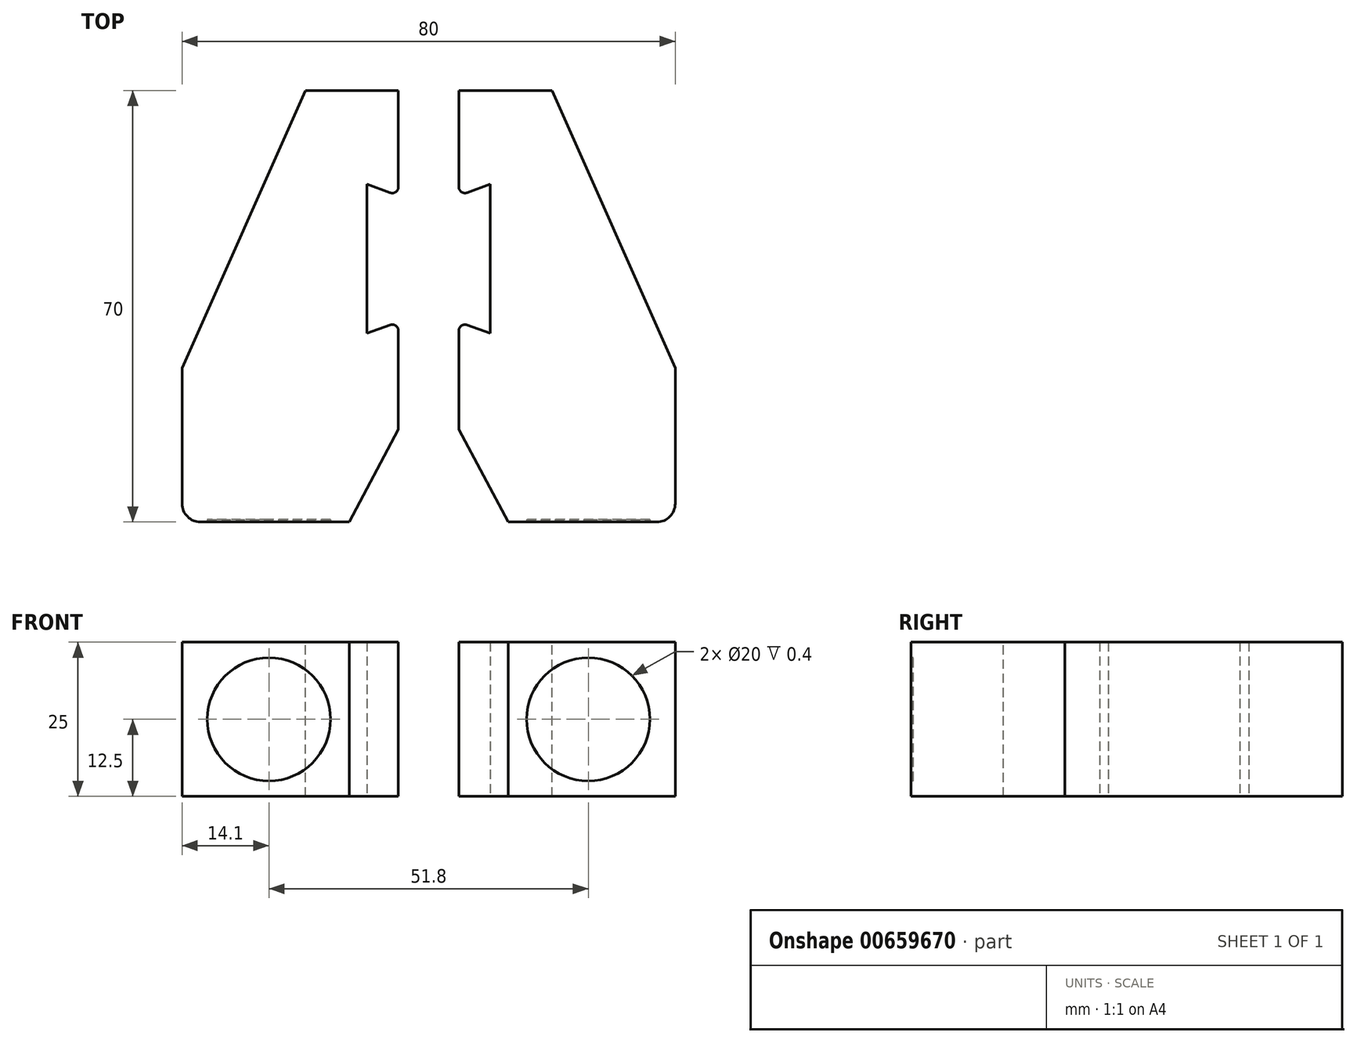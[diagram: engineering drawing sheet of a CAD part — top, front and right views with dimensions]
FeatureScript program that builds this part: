
annotation { "Feature Type Name" : "Feature", "Feature Type Description" : "" }
export const myFeature = defineFeature(function(context is Context, id is Id, definition is map)
    precondition{}
    {
        {
            var Q0;
            Q0=qCreatedBy(makeId("Top.planeOp"),FACE);
            var sketch = newSketch(context, id + "F0", { "sketchPlane" : qUnion([Q0])});
            skLineSegment(sketch, "E0.bottom", {"start": v(-15, 27.5) * mm, "end": v(15, 27.5) * mm});
            skLineSegment(sketch, "E0.top", {"start": v(-15, -27.5) * mm, "end": v(15, -27.5) * mm});
            skLineSegment(sketch, "E0.left", {"start": v(-15, 27.5) * mm, "end": v(-15, -27.5) * mm});
            skLineSegment(sketch, "E0.right", {"start": v(15, 27.5) * mm, "end": v(15, -27.5) * mm});
            skPoint(sketch, "E0.middle", {"position": v(0, 0) * mm});
            skLineSegment(sketch, "E1", {"start": v(-15, 27.5) * mm, "end": v(-20.1, 27.5) * mm});
            skLineSegment(sketch, "E2", {"start": v(-20.1, 27.5) * mm, "end": v(-20.1, 10.44) * mm});
            skLineSegment(sketch, "E3", {"start": v(-20.1, 10.44) * mm, "end": v(-15, 12.3) * mm});
            skLineSegment(sketch, "E4", {"start": v(-15, -11.9) * mm, "end": v(-20.1, -10.04) * mm});
            skLineSegment(sketch, "E5", {"start": v(-20.1, -10.04) * mm, "end": v(-20.1, -27.5) * mm});
            skLineSegment(sketch, "E6", {"start": v(-20.1, -27.5) * mm, "end": v(-15, -27.5) * mm});
            skSolve(sketch);
        }
        {
            var Q0;
            Q0 = qSketchRegion(id + "F0", true);
            extrude(context, id + "F1", {"entities" : qUnion([Q0]), "depth" : 25 * mm, "offsetDistance" : 25 * mm});
        }
        {
            var Q0;
            Q0=makeQuery(id+"F1.opExtrude","SWEPT_FACE",FACE,{"disambiguationData":[OSD([sQuery(id+"F0.wireOp",EDGE,"E0.top"),sQuery(id+"F0.wireOp",EDGE,"E6")])]});
            extrude(context, id + "F2", {"entities" : qUnion([Q0]), "operationType" : NewBodyOperationType.ADD, "depth" : 15 * mm, "offsetDistance" : 25 * mm});
        }
        {
            var Q0;
            Q0=makeQuery(id+"F2.opExtrude","CAP_FACE",FACE,{"disambiguationData":[OSD([sQuery(id+"F0.wireOp",EDGE,"E0.top"),sQuery(id+"F0.wireOp",EDGE,"E6")])],"isStart":false});
            var sketch = newSketch(context, id + "F3", { "sketchPlane" : qUnion([Q0])});
            skPoint(sketch, "E7", {"position": v(-20.1, 12.5) * mm});
            skCircle(sketch, "E8", {"center": v(0.9, 12.5) * mm, "radius": 10 * mm});
            skSolve(sketch);
        }
        {
            var Q0;
            Q0 = qSketchRegion(id + "F3", true);
            extrude(context, id + "F4", {"entities" : qUnion([Q0]), "operationType" : NewBodyOperationType.REMOVE, "oppositeDirection" : true, "depth" : 0.4 * mm, "offsetDistance" : 25 * mm});
        }
        {
            var Q0;
            {var subQ0=sQuery(id+"F0.wireOp",EDGE,"E6");var subQ1=sQuery(id+"F0.wireOp",EDGE,"E0.top");Q0=makeQuery(id+"F2.boolean.opBoolean","MERGE",FACE,{"derivedFrom":[makeQuery(id+"F1.opExtrude","CAP_FACE",FACE,{"disambiguationData":[OSD([sQuery(id+"F0.wireOp",EDGE,"E0.bottom"),subQ1,sQuery(id+"F0.wireOp",EDGE,"E0.left"),sQuery(id+"F0.wireOp",EDGE,"E0.right"),sQuery(id+"F0.wireOp",EDGE,"E1"),sQuery(id+"F0.wireOp",EDGE,"E2"),sQuery(id+"F0.wireOp",EDGE,"E3"),sQuery(id+"F0.wireOp",EDGE,"E4"),sQuery(id+"F0.wireOp",EDGE,"E5"),subQ0])],"isStart":false}),makeQuery(id+"F2.opExtrude","SWEPT_FACE",FACE,{"disambiguationData":[OSD([subQ1,subQ0]),TDD([makeQuery(id+"F1.opExtrude","CAP_EDGE",EDGE,{"disambiguationData":[OSD([subQ1,subQ0])],"isStart":false})])]})]});}
            var sketch = newSketch(context, id + "F5", { "sketchPlane" : qUnion([Q0])});
            skLineSegment(sketch, "E9", {"start": v(15, 27.5) * mm, "end": v(-5, 27.5) * mm});
            skLineSegment(sketch, "E10", {"start": v(-5, 27.5) * mm, "end": v(15, -17.5) * mm});
            skLineSegment(sketch, "E11", {"start": v(15, -17.5) * mm, "end": v(15, 27.5) * mm});
            skLineSegment(sketch, "E12", {"start": v(-20.1, -42.5) * mm, "end": v(-12.1, -42.5) * mm});
            skLineSegment(sketch, "E13", {"start": v(-12.1, -42.5) * mm, "end": v(-20.1, -27.5) * mm});
            skLineSegment(sketch, "E14", {"start": v(-20.1, -27.5) * mm, "end": v(-20.1, -42.5) * mm});
            skSolve(sketch);
        }
        {
            var Q0;
            Q0 = qSketchRegion(id + "F5", true);
            extrude(context, id + "F6", {"entities" : qUnion([Q0]), "operationType" : NewBodyOperationType.REMOVE, "oppositeDirection" : true, "depth" : 25 * mm, "offsetDistance" : 25 * mm});
        }
        {
            var Q0;
            Q0=qCreatedBy(makeId("Right.planeOp"),FACE);
            cPlane(context, id + "F7", {"entities" : qUnion([Q0]), "cplaneType" : CPlaneType.OFFSET, "offset" : 25 * mm, "oppositeDirection" : true, "width" : 150 * mm, "height" : 150 * mm});
        }
        {
            var Q0;
            Q0=makeQuery(id+"F1.opExtrude","SWEPT_BODY",BODY,{"disambiguationData":[OSD([sQuery(id+"F0.wireOp",EDGE,"E0.bottom"),sQuery(id+"F0.wireOp",EDGE,"E0.top"),sQuery(id+"F0.wireOp",EDGE,"E0.left"),sQuery(id+"F0.wireOp",EDGE,"E0.right"),sQuery(id+"F0.wireOp",EDGE,"E1"),sQuery(id+"F0.wireOp",EDGE,"E2"),sQuery(id+"F0.wireOp",EDGE,"E3"),sQuery(id+"F0.wireOp",EDGE,"E4"),sQuery(id+"F0.wireOp",EDGE,"E5"),sQuery(id+"F0.wireOp",EDGE,"E6")])]});
            var Q1;
            Q1=qCreatedBy(id+"F7.planeOp",FACE);
            mirror(context, id + "F8", {"entities" : qUnion([Q0]), "mirrorPlane" : qUnion([Q1])});
        }
        {
            var Q0;
            Q0=makeQuery(id+"F8.opPattern","COPY",EDGE,{"derivedFrom":makeQuery(id+"F1.opExtrude","SWEPT_EDGE",EDGE,{"disambiguationData":[OSD([sQuery(id+"F0.wireOp",EDGE,"E2"),sQuery(id+"F0.wireOp",EDGE,"E3")])]}),"instanceName":"1"});
            var Q1;
            Q1=makeQuery(id+"F1.opExtrude","SWEPT_EDGE",EDGE,{"disambiguationData":[OSD([sQuery(id+"F0.wireOp",EDGE,"E2"),sQuery(id+"F0.wireOp",EDGE,"E3")])]});
            var Q2;
            Q2=makeQuery(id+"F8.opPattern","COPY",EDGE,{"derivedFrom":makeQuery(id+"F1.opExtrude","SWEPT_EDGE",EDGE,{"disambiguationData":[OSD([sQuery(id+"F0.wireOp",EDGE,"E4"),sQuery(id+"F0.wireOp",EDGE,"E5")])]}),"instanceName":"1"});
            var Q3;
            Q3=makeQuery(id+"F1.opExtrude","SWEPT_EDGE",EDGE,{"disambiguationData":[OSD([sQuery(id+"F0.wireOp",EDGE,"E4"),sQuery(id+"F0.wireOp",EDGE,"E5")])]});
            fillet(context, id + "F9", {"entities" : qUnion([Q0, Q1, Q2, Q3]), "tangentPropagation" : true, "radius" : 1 * mm, "defaultsChanged" : false, "vertexSettings" : [], "allowEdgeOverflow" : false});
        }
        {
            var Q0;
            Q0=makeQuery(id+"F8.opPattern","COPY",EDGE,{"derivedFrom":makeQuery(id+"F2.opExtrude","CAP_EDGE",EDGE,{"disambiguationData":[OSD([sQuery(id+"F0.wireOp",EDGE,"E0.top"),sQuery(id+"F0.wireOp",EDGE,"E0.right")])],"isStart":false}),"instanceName":"1"});
            var Q1;
            Q1=makeQuery(id+"F2.opExtrude","CAP_EDGE",EDGE,{"disambiguationData":[OSD([sQuery(id+"F0.wireOp",EDGE,"E0.top"),sQuery(id+"F0.wireOp",EDGE,"E0.right")])],"isStart":false});
            var Q2;
            Q2=makeQuery(id+"F6.boolean.opBoolean","COPY",EDGE,{"derivedFrom":makeQuery(id+"F6.opExtrude","SWEPT_EDGE",EDGE,{"disambiguationData":[OSD([sQuery(id+"F0.wireOp",EDGE,"E0.bottom"),sQuery(id+"F0.wireOp",EDGE,"E1"),sQuery(id+"F5.wireOp",EDGE,"E9"),sQuery(id+"F5.wireOp",EDGE,"E10")])]})});
            var Q3;
            Q3=makeQuery(id+"F8.opPattern","COPY",EDGE,{"derivedFrom":makeQuery(id+"F6.boolean.opBoolean","COPY",EDGE,{"derivedFrom":makeQuery(id+"F6.opExtrude","SWEPT_EDGE",EDGE,{"disambiguationData":[OSD([sQuery(id+"F0.wireOp",EDGE,"E0.bottom"),sQuery(id+"F0.wireOp",EDGE,"E1"),sQuery(id+"F5.wireOp",EDGE,"E9"),sQuery(id+"F5.wireOp",EDGE,"E10")])]})}),"instanceName":"1"});
            var Q4;
            Q4=makeQuery(id+"F8.opPattern","COPY",EDGE,{"derivedFrom":makeQuery(id+"F6.boolean.opBoolean","COPY",EDGE,{"derivedFrom":makeQuery(id+"F6.opExtrude","SWEPT_EDGE",EDGE,{"disambiguationData":[OSD([sQuery(id+"F0.wireOp",EDGE,"E0.top"),sQuery(id+"F0.wireOp",EDGE,"E6"),sQuery(id+"F5.wireOp",EDGE,"E12"),sQuery(id+"F5.wireOp",EDGE,"E13")])]})}),"instanceName":"1"});
            var Q5;
            Q5=makeQuery(id+"F6.boolean.opBoolean","COPY",EDGE,{"derivedFrom":makeQuery(id+"F6.opExtrude","SWEPT_EDGE",EDGE,{"disambiguationData":[OSD([sQuery(id+"F0.wireOp",EDGE,"E0.top"),sQuery(id+"F0.wireOp",EDGE,"E6"),sQuery(id+"F5.wireOp",EDGE,"E12"),sQuery(id+"F5.wireOp",EDGE,"E13")])]})});
            fillet(context, id + "F10", {"entities" : qUnion([Q0, Q1, Q2, Q3, Q4, Q5]), "tangentPropagation" : true, "radius" : 3 * mm, "defaultsChanged" : false, "vertexSettings" : [], "allowEdgeOverflow" : false});
        }
    });
